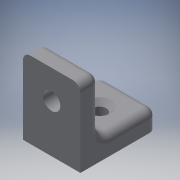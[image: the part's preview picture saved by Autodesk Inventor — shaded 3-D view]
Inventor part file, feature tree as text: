
AUTODESK INVENTOR PART (.ipt)
format: ipt  version: 2016 (Build 200138000, 138)  size: 162,304 bytes
history: native  units: mm
features: extrude x3, sketch x3, chamfer x2, fillet x2, projected_geometry x2
ambient origin geometry x8: Origin, YZ Plane, XZ Plane, XY Plane, X Axis, Y Axis, Z Axis, Center Point
bodies: Solid1 (feature_tree)
feature tree (12):
  extrude  "Extrusion1"  Depth=5.0mm
  extrude  "Extrusion2"  Depth=20.0mm
  extrude  "Extrusion3"  Depth=2.0mm
  chamfer  "Chamfer1"  Distance=12.5mm
  chamfer  "Chamfer2"  Distance=15.0mm
  fillet  "Fillet1"  Radius=3.5mm
  fillet  "Fillet2"  Radius=15.0mm
  sketch  "Sketch1"  dims[d0=20.0mm d1=5.0mm]
  sketch  "Sketch2"  dims[d2=5.0mm d3=20.0mm]
  projected_geometry  "Projected Loop1"
  sketch  "Sketch3"  dims[d4=15.0mm d5=0.0mm d6=4.5mm d7=12.5mm d8=15.0mm d9=0.0mm d10=3.5mm d11=15.0mm d12=0.0mm d13=1.25mm d14=2.0mm d15=45.0deg d16=1.5mm d17=2.0mm d18=45.0deg d19=3.0mm d21=2.0mm]
  projected_geometry  "Projected Loop2"
